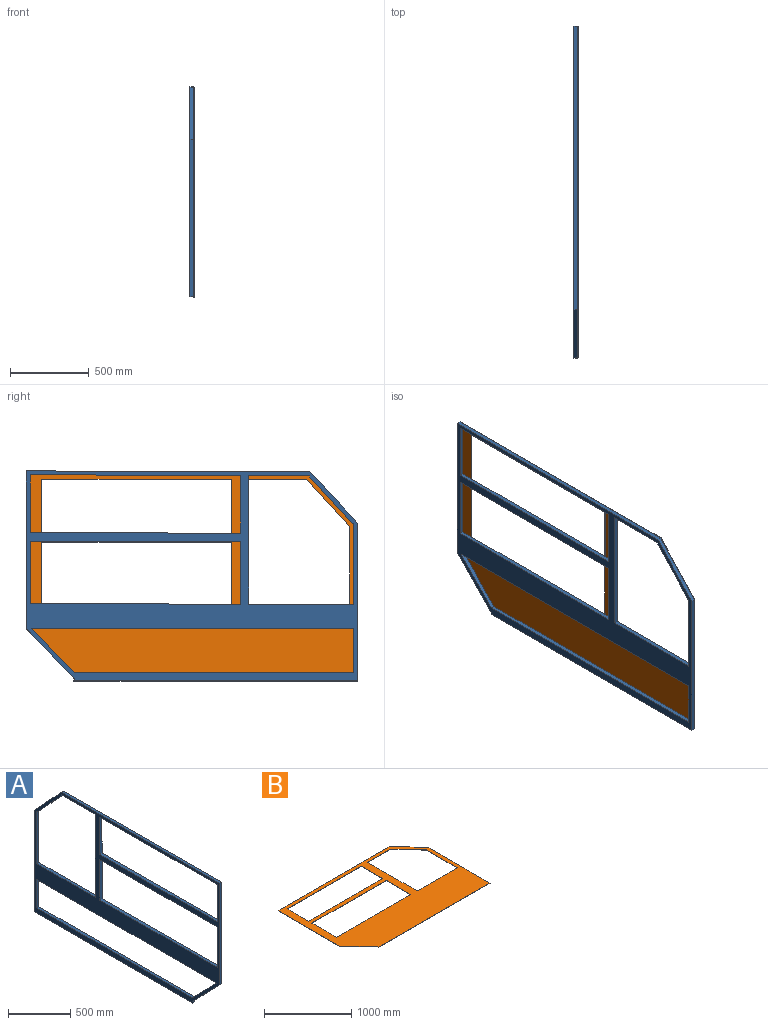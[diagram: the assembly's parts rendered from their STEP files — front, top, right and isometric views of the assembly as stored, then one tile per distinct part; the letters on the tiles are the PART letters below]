
ASSEMBLY  parts=2 mates=1
PART A: 28 faces, bbox 25x2103.6x1331.6 mm
  f0: plane 366.41x25mm, normal (0,1,0), area 9160.2mm2, adj f1,f25,f26,f27
  f1: plane 1335.61x25mm, normal (0,0,-1), area 33390.3mm2, adj f0,f2,f26,f27
  f2: plane 367.68x25mm, normal (0,-1,0), area 9192.1mm2, adj f1,f25,f26,f27
  f3: plane 397.98x25mm, normal (0,1,0), area 9949.5mm2, adj f4,f21,f26,f27
  f4: plane 1335x25mm, normal (0,0,-1), area 33375mm2, adj f3,f5,f26,f27
  f5: plane 399.94x25mm, normal (0,-1,0), area 9998.4mm2, adj f4,f21,f26,f27
  f6: plane 328.96x303.65mm, normal (0,0.73,0.68), area 11192mm2, adj f7,f22,f26,f27
  f7: plane 1800x25mm, normal (0,0,1), area 45000mm2, adj f6,f8,f26,f27
  f8: plane 1000x25mm, normal (0,-1,0), area 25000mm2, adj f7,f9,f26,f27
  f9: plane 317.79x303.64mm, normal (0,-0.72,-0.69), area 10988.3mm2, adj f8,f10,f26,f27
  f10: plane 25x13.81mm, normal (0,-1,0), area 345.3mm2, adj f9,f11,f26,f27
  f11: plane 1800x25mm, normal (0,0,-1), area 45000mm2, adj f10,f22,f26,f27
  f12: plane 281.6x269.07mm, normal (0,0.72,0.69), area 9737mm2, adj f13,f23,f26,f27
  f13: plane 2044.07x25mm, normal (0,0,-1), area 51101.7mm2, adj f12,f14,f26,f27
  f14: plane 281.6x25mm, normal (0,-1,0), area 7040mm2, adj f13,f23,f26,f27
  f15: plane 668.03x25mm, normal (0,0,1), area 16700.9mm2, adj f16,f24,f26,f27
  f16: plane 817.61x25mm, normal (0,1,0), area 20440.2mm2, adj f15,f17,f26,f27
  f17: plane 389.39x25mm, normal (0,0,-1), area 9734.7mm2, adj f16,f18,f26,f27
  f18: plane 25x11.86mm, normal (0,-1,0), area 296.5mm2, adj f17,f19,f26,f27
  f19: plane 292.1x269.62mm, normal (0,-0.73,-0.68), area 9938mm2, adj f18,f20,f26,f27
  f20: plane 25x9.02mm, normal (0,0,-1), area 225.6mm2, adj f19,f24,f26,f27
  f21: plane 1334.41x25mm, normal (0,0,1), area 33360.3mm2, adj f3,f5,f26,f27
  f22: plane 1000x25mm, normal (0,1,0), area 25000mm2, adj f6,f11,f26,f27
  f23: plane 1775x25mm, normal (0,0,1), area 44375mm2, adj f12,f14,f26,f27
  f24: plane 514.06x25mm, normal (0,-1,0), area 12851.4mm2, adj f15,f20,f26,f27
  f25: plane 1335.07x25mm, normal (0,0,1), area 33376.9mm2, adj f0,f2,f26,f27
  f26: plane 2103.64x1331.6mm, normal (1,0,0), area 634376.3mm2, adj f0,f1,f2,f3,f4,f5,f6,f7
  f27: plane 2103.64x1331.6mm, normal (-1,0,0), area 634376.3mm2, adj f0,f1,f2,f3,f4,f5,f6,f7
PART B: 22 faces, bbox 2102.5x1330x3 mm
  f0: plane 650x3mm, normal (0,1,0), area 1950mm2, adj f1,f19,f20,f21
  f1: plane 800x3mm, normal (1,0,0), area 2400mm2, adj f0,f2,f20,f21
  f2: plane 375.49x3mm, normal (0,-1,0), area 1126.5mm2, adj f1,f3,f20,f21
  f3: plane 299.45x274.51mm, normal (-0.74,-0.68,0), area 1218.7mm2, adj f2,f19,f20,f21
  f4: plane 1200x3mm, normal (0,-1,0), area 3600mm2, adj f5,f16,f20,f21
  f5: plane 350x3mm, normal (-1,0,0), area 1050mm2, adj f4,f6,f20,f21
  f6: plane 1200x3mm, normal (0,1,0), area 3600mm2, adj f5,f16,f20,f21
  f7: plane 1200x3mm, normal (0,-1,0), area 3600mm2, adj f8,f17,f20,f21
  f8: plane 400x3mm, normal (-1,0,0), area 1200mm2, adj f7,f9,f20,f21
  f9: plane 1200x3mm, normal (0,1,0), area 3600mm2, adj f8,f17,f20,f21
  f10: plane 26.12x3mm, normal (-1,0,0), area 78.4mm2, adj f11,f18,f20,f21
  f11: plane 1800x3mm, normal (0,-1,0), area 5400mm2, adj f10,f12,f20,f21
  f12: plane 1000x3mm, normal (1,0,0), area 3000mm2, adj f11,f13,f20,f21
  f13: plane 330x302.52mm, normal (0.74,0.68,0), area 1343mm2, adj f12,f14,f20,f21
  f14: plane 1800x3mm, normal (0,1,0), area 5400mm2, adj f13,f15,f20,f21
  f15: plane 1000x3mm, normal (-1,0,0), area 3000mm2, adj f14,f18,f20,f21
  f16: plane 350x3mm, normal (1,0,0), area 1050mm2, adj f4,f6,f20,f21
  f17: plane 400x3mm, normal (1,0,0), area 1200mm2, adj f7,f9,f20,f21
  f18: plane 303.88x302.52mm, normal (-0.71,-0.71,0), area 1286.4mm2, adj f10,f15,f20,f21
  f19: plane 500.55x3mm, normal (-1,0,0), area 1501.7mm2, adj f0,f3,f20,f21
  f20: plane 2102.52x1330mm, normal (0,0,1), area 1313666.5mm2, adj f0,f1,f2,f3,f4,f5,f6,f7
  f21: plane 2102.52x1330mm, normal (0,0,-1), area 1313666.5mm2, adj f0,f1,f2,f3,f4,f5,f6,f7
PLACE A rot(axis=(0,0,1),180deg) t=(13.84,-1491.14,-5812.58)mm
PLACE B rot(axis=(0.58,-0.58,-0.58),120deg) t=(16.84,-487.12,241.42)mm
MATE fastened A.f27 <-> B.f20  axis (1,0,0) through (13.84,-1603.18,794.73)mm
